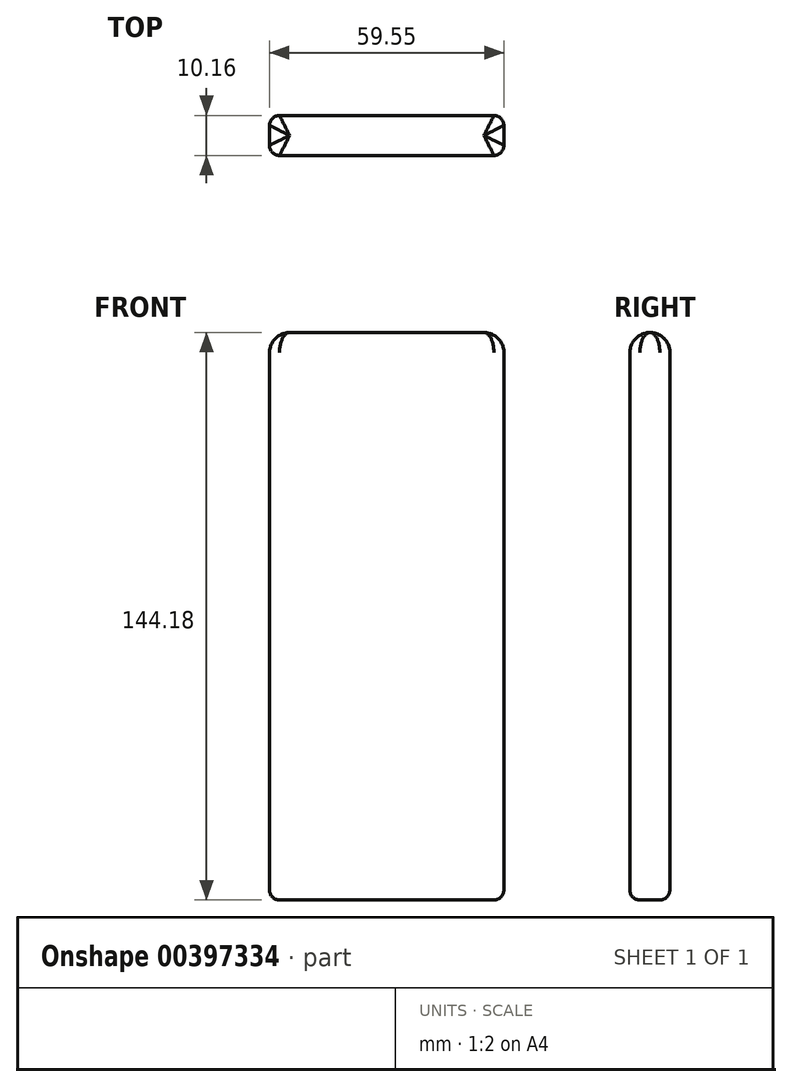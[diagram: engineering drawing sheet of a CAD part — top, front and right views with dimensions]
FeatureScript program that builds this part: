
annotation { "Feature Type Name" : "Feature", "Feature Type Description" : "" }
export const myFeature = defineFeature(function(context is Context, id is Id, definition is map)
    precondition{}
    {
        {
            var Q0;
            Q0=qCreatedBy(makeId("Front.planeOp"),FACE);
            var sketch = newSketch(context, id + "F0", { "sketchPlane" : qUnion([Q0])});
            skLineSegment(sketch, "E0.bottom", {"start": v(-46.06, -76.46) * mm, "end": v(13.49, -76.46) * mm});
            skLineSegment(sketch, "E0.top", {"start": v(-46.06, 67.72) * mm, "end": v(13.49, 67.72) * mm});
            skLineSegment(sketch, "E0.left", {"start": v(-46.06, -76.46) * mm, "end": v(-46.06, 67.72) * mm});
            skLineSegment(sketch, "E0.right", {"start": v(13.49, -76.46) * mm, "end": v(13.49, 67.72) * mm});
            skSolve(sketch);
        }
        {
            var Q0;
            Q0=makeQuery(id+"F0.imprint","IMPRINT",FACE,{"disambiguationData":[TD([[makeQuery(id+"F0.imprint","IMPRINT",EDGE,{"derivedFrom":sQuery(id+"F0.wireOp",EDGE,"E0.bottom")}),1.0]])]});
            extrude(context, id + "F1", {"entities" : qUnion([Q0]), "depth" : 10.16 * mm});
        }
        {
            var Q0;
            Q0=makeQuery(id+"F1.opExtrude","CAP_EDGE",EDGE,{"disambiguationData":[OSD([sQuery(id+"F0.wireOp",EDGE,"E0.right")])],"isStart":false});
            fillet(context, id + "F2", {"entities" : qUnion([Q0]), "radius" : 2.54 * mm, "tangentPropagation" : true, "allowEdgeOverflow" : false});
        }
        {
            var Q0;
            Q0=makeQuery(id+"F1.opExtrude","CAP_EDGE",EDGE,{"disambiguationData":[OSD([sQuery(id+"F0.wireOp",EDGE,"E0.right")])],"isStart":true});
            fillet(context, id + "F3", {"entities" : qUnion([Q0]), "radius" : 2.54 * mm, "tangentPropagation" : true, "allowEdgeOverflow" : false});
        }
        {
            var Q0;
            Q0=makeQuery(id+"F1.opExtrude","CAP_EDGE",EDGE,{"disambiguationData":[OSD([sQuery(id+"F0.wireOp",EDGE,"E0.left")])],"isStart":false});
            var Q1;
            Q1=makeQuery(id+"F1.opExtrude","CAP_EDGE",EDGE,{"disambiguationData":[OSD([sQuery(id+"F0.wireOp",EDGE,"E0.left")])],"isStart":true});
            fillet(context, id + "F4", {"entities" : qUnion([Q0, Q1]), "radius" : 2.54 * mm, "tangentPropagation" : true, "allowEdgeOverflow" : false});
        }
        {
            var Q0;
            Q0=makeQuery(id+"F1.opExtrude","CAP_EDGE",EDGE,{"disambiguationData":[OSD([sQuery(id+"F0.wireOp",EDGE,"E0.top")])],"isStart":true});
            fillet(context, id + "F5", {"entities" : qUnion([Q0]), "radius" : 5.08 * mm, "tangentPropagation" : true, "allowEdgeOverflow" : false});
        }
        {
            var Q0;
            Q0=makeQuery(id+"F1.opExtrude","CAP_EDGE",EDGE,{"disambiguationData":[OSD([sQuery(id+"F0.wireOp",EDGE,"E0.bottom")])],"isStart":true});
            fillet(context, id + "F6", {"entities" : qUnion([Q0]), "radius" : 2.54 * mm, "tangentPropagation" : true, "allowEdgeOverflow" : false});
        }
    });
